FCSTD DOCUMENT  (FreeCAD 0.19R)
Label: threaded_ass2
License: All rights reserved
LicenseURL: http://en.wikipedia.org/wiki/All_rights_reserved
objects: Part::FeaturePython×42, Part::Feature×40, Part::Compound×26
note: 108 computed .brp shape members not serialized (recipe doc carries the construction recipe); baked Part::Feature solids carry a one-line shape summary decoded from their .brp

FEATURE [Part::Feature] Fillet001  label="endplate1b_chamf"
  shape: bbox 100 x 64 x 15 mm, 27 faces (baked)
FEATURE [Part::Feature] Fillet002  label="mountplate3b_chamf"
  Placement = pos=(0,0,455) rot=(0,0,1;0rad)
  shape: bbox 100 x 64 x 15 mm, 39 faces (baked)
FEATURE [Part::Feature] Pad001  label="shaft8x480"
  Placement = pos=(18,42.85,-5) rot=(0,0,1;0rad)
  shape: bbox 8 x 8 x 480 mm, 3 faces (baked)
FEATURE [Part::Feature] Pad002  label="shaft8x481"
  Placement = pos=(82,42.85,-5) rot=(0,0,1;0rad)
  shape: bbox 8 x 8 x 480 mm, 3 faces (baked)
FEATURE [Part::Feature] Fusion001  label="trapthread"
  Placement = pos=(50,42.85,-42) rot=(0,0,1;0rad)
  shape: bbox 12.27 x 13.21 x 480 mm, 558 faces (baked)
FEATURE [Part::Feature] Fusion001001001  label="nema17"
  Placement = pos=(50,42.85,510) rot=(0,1,0;3.14159rad)
  shape: bbox 48 x 42.3 x 60.1 mm, 110 faces (baked)
FEATURE [Part::Feature] Chamfer001  label="608zz"
  Placement = pos=(50,42.85,11) rot=(1,0,0;1.5708rad)
  shape: bbox 22 x 22 x 7 mm, 14 faces (baked)
FEATURE [Part::Feature] Body007  label="m6nutplate005"
  Placement = pos=(15,15,-3.5) rot=(0,0,-1;1.5708rad)
  shape: bbox 10 x 10 x 3 mm, 9 faces (baked)
FEATURE [Part::FeaturePython] b_tslot40_001_007  label="tslot40_Pocket001_008"  # a2plus imported part (geometry in sourceFile) (typed FeaturePython)
  Placement = pos=(60,10,15) rot=(-1,0,0;1.5708rad)
  Visibility1 = false
  Visibility11 = true
  a2p_Version = V0.1
  fixedPosition = false
  objectType = a2pPart
  sourceFile = .\Neuer Ordner (3)\tslot40.fcstd
  sourcePart = Pocket001
  subassemblyImport = false
  timeLastImport = 1585500225
  updateColors = true
FEATURE [Part::Feature] Body008  label="m6nutplate006"
  Placement = pos=(15,15,-3.5) rot=(0,0,-1;1.5708rad)
  shape: bbox 10 x 10 x 3 mm, 9 faces (baked)
FEATURE [Part::Feature] Pocket004003  label="tslot8con002"
  Placement = pos=(70,10,5) rot=(0,-1,0;1.5708rad)
  shape: bbox 80 x 20 x 20 mm, 150 faces (baked)
FEATURE [Part::Feature] Screw009  label="M6x16-Screw005"
  Placement = pos=(20,10,-16) rot=(1,0,0;3.14159rad)
  shape: bbox 10.5 x 10.5 x 19.3 mm, 15 faces (baked)
FEATURE [Part::Compound] Compound006  label="nutscrew020"
  Links = -> [Screw009,Body007]
  Placement = pos=(20,20,430) rot=(1,0,0;3.14159rad)
FEATURE [Part::FeaturePython] b_tslot40_001_010  label="tslot40_Pocket001_011"  # a2plus imported part (geometry in sourceFile) (typed FeaturePython)
  Placement = pos=(0,10,15) rot=(-1,0,0;1.5708rad)
  Visibility1 = false
  Visibility11 = true
  a2p_Version = V0.1
  fixedPosition = false
  objectType = a2pPart
  sourceFile = .\Neuer Ordner (3)\tslot40.fcstd
  sourcePart = Pocket001
  subassemblyImport = false
  timeLastImport = 1585500225
  updateColors = true
FEATURE [Part::Feature] Screw010  label="M6x16-Screw006"
  Placement = pos=(20,10,-16) rot=(1,0,0;3.14159rad)
  shape: bbox 10.5 x 10.5 x 19.3 mm, 15 faces (baked)
FEATURE [Part::Feature] Screw011  label="M6x40-Screw005"
  Placement = pos=(0,10,444) rot=(0,0,1;0rad)
  shape: bbox 10 x 10 x 46 mm, 19 faces (baked)
FEATURE [Part::Feature] Screw012  label="M6x40-Screw006"
  Placement = pos=(60,10,444) rot=(0,0,1;0rad)
  shape: bbox 10 x 10 x 46 mm, 19 faces (baked)
FEATURE [Part::Feature] Body009  label="m6nutplate007"
  Placement = pos=(15,15,-3.5) rot=(0,0,-1;1.5708rad)
  shape: bbox 10 x 10 x 3 mm, 9 faces (baked)
FEATURE [Part::Feature] Pocket004004  label="tslot8con003"
  Placement = pos=(70,10,425) rot=(0.707107,0,-0.707107;3.14159rad)
  shape: bbox 80 x 20 x 20 mm, 150 faces (baked)
FEATURE [Part::Feature] Body010  label="m6nutplate008"
  Placement = pos=(15,15,-3.5) rot=(0,0,-1;1.5708rad)
  shape: bbox 10 x 10 x 3 mm, 9 faces (baked)
FEATURE [Part::Compound] Compound009  label="nutscrew023"
  Links = -> [Screw010,Body010]
FEATURE [Part::Feature] Screw013  label="M6x40-Screw007"
  Placement = pos=(0,10,-14) rot=(1,0,0;3.14159rad)
  shape: bbox 10 x 10 x 46 mm, 19 faces (baked)
FEATURE [Part::Feature] Screw014  label="M6x40-Screw008"
  Placement = pos=(60,10,-14) rot=(1,0,0;3.14159rad)
  shape: bbox 10 x 10 x 46 mm, 19 faces (baked)
FEATURE [Part::Feature] Screw015  label="M6x16-Screw007"
  Placement = pos=(20,10,-16) rot=(1,0,0;3.14159rad)
  shape: bbox 10.5 x 10.5 x 19.3 mm, 15 faces (baked)
FEATURE [Part::Compound] Compound008  label="nutscrew022"
  Links = -> [Screw015,Body008]
  Placement = pos=(0,20,430) rot=(1,0,0;3.14159rad)
FEATURE [Part::Feature] Screw016  label="M6x16-Screw008"
  Placement = pos=(20,10,-16) rot=(1,0,0;3.14159rad)
  shape: bbox 10.5 x 10.5 x 19.3 mm, 15 faces (baked)
FEATURE [Part::Compound] Compound007  label="nutscrew021"
  Links = -> [Screw016,Body009]
  Placement = pos=(20,0,0) rot=(0,0,1;0rad)
FEATURE [Part::Compound] Compound010  label="frame_ass"
  Links = -> [b_tslot40_001_007,b_tslot40_001_010,Pocket004003,Pocket004004,Screw011,Screw012,Screw014,Screw013,Compound009,Compound007,Compound006,Compound008]
  Placement = pos=(20,0,20) rot=(0,0,1;0rad)
FEATURE [Part::Feature] difference001001  label="shaftcollar8mm"
  Placement = pos=(18,43,470) rot=(0,0,1;0rad)
  shape: bbox 20 x 19.97 x 8 mm, 16 faces (baked)
FEATURE [Part::Feature] difference001002  label="shaftcollar8mm001"
  Placement = pos=(82,43,470) rot=(0,0,1;0rad)
  shape: bbox 20 x 19.97 x 8 mm, 16 faces (baked)
FEATURE [Part::Feature] difference001003  label="shaftcollar8mm002"
  Placement = pos=(18,43,446.8) rot=(0,0,1;0rad)
  shape: bbox 20 x 19.97 x 8 mm, 16 faces (baked)
FEATURE [Part::Feature] difference001004  label="shaftcollar8mm003"
  Placement = pos=(82,43,446.8) rot=(0,0,1;0rad)
  shape: bbox 20 x 19.97 x 8 mm, 16 faces (baked)
FEATURE [Part::Feature] difference001005  label="shaftcollar8mm004"
  Placement = pos=(18,43,470) rot=(0,0,1;0rad)
  shape: bbox 20 x 19.97 x 8 mm, 16 faces (baked)
FEATURE [Part::Feature] difference001006  label="shaftcollar8mm005"
  Placement = pos=(82,43,470) rot=(0,0,1;0rad)
  shape: bbox 20 x 19.97 x 8 mm, 16 faces (baked)
FEATURE [Part::Feature] difference001007  label="shaftcollar8mm006"
  Placement = pos=(18,43,446.8) rot=(0,0,1;0rad)
  shape: bbox 20 x 19.97 x 8 mm, 16 faces (baked)
FEATURE [Part::Feature] difference001008  label="shaftcollar8mm007"
  Placement = pos=(82,43,446.8) rot=(0,0,1;0rad)
  shape: bbox 20 x 19.97 x 8 mm, 16 faces (baked)
FEATURE [Part::Compound] Compound  label="shaftcollars"
  Links = -> [difference001005,difference001006,difference001007,difference001008]
  Placement = pos=(0,0,-455) rot=(0,0,1;0rad)
FEATURE [Part::Compound] Compound011  label="shaftcollars2"
  Links = -> [difference001001,difference001002,difference001003,difference001004]
FEATURE [Part::FeaturePython] Screw  label="M3x16-Screw"  # Fasteners workbench fastener (typed FeaturePython)
  Placement = pos=(34.5,27,458) rot=(0,1,0;3.14159rad)
  Visibility1 = false
  diameter = 4
  invert = false
  length = 6
  matchOuter = false
  offset = 0
  thread = false
  type = 15
FEATURE [Part::FeaturePython] Screw017  label="M3x16-Screw001"  # Fasteners workbench fastener (typed FeaturePython)
  Placement = pos=(65.5,27,458) rot=(0,1,0;3.14159rad)
  Visibility1 = false
  diameter = 4
  invert = false
  length = 6
  matchOuter = false
  offset = 0
  thread = false
  type = 15
FEATURE [Part::FeaturePython] Screw018  label="M3x16-Screw002"  # Fasteners workbench fastener (typed FeaturePython)
  Placement = pos=(34.5,58,458) rot=(0,1,0;3.14159rad)
  Visibility1 = false
  diameter = 4
  invert = false
  length = 6
  matchOuter = false
  offset = 0
  thread = false
  type = 15
FEATURE [Part::FeaturePython] Screw019  label="M3x16-Screw003"  # Fasteners workbench fastener (typed FeaturePython)
  Placement = pos=(65.5,58,458) rot=(0,1,0;3.14159rad)
  Visibility1 = false
  diameter = 4
  invert = false
  length = 6
  matchOuter = false
  offset = 0
  thread = false
  type = 15
FEATURE [Part::Compound] Compound012  label="m3x16s"
  Links = -> [Screw,Screw017,Screw018,Screw019]
FEATURE [Part::FeaturePython] Screw020  label="M4x35-Screw001"  # Fasteners workbench fastener (typed FeaturePython)
  Placement = pos=(65,37,6) rot=(0,0,1;0rad)
  Visibility1 = false
  diameter = 5
  invert = false
  length = 9
  matchOuter = false
  offset = 0
  thread = false
  type = 15
FEATURE [Part::FeaturePython] Screw021  label="M4x12-Screw011"  # Fasteners workbench fastener (typed FeaturePython)
  Placement = pos=(6,6,6) rot=(0,0,1;0rad)
  Visibility1 = false
  diameter = 5
  invert = false
  length = 3
  matchOuter = false
  offset = 0
  thread = false
  type = 15
FEATURE [Part::FeaturePython] Screw022  label="M4x12-Screw014"  # Fasteners workbench fastener (typed FeaturePython)
  Placement = pos=(30,24,6) rot=(0,0,1;0rad)
  Visibility1 = false
  diameter = 5
  invert = false
  length = 3
  matchOuter = false
  offset = 0
  thread = false
  type = 15
FEATURE [Part::FeaturePython] Nut010  label="M3-Nut002"  # Fasteners workbench fastener (typed FeaturePython)
  Placement = pos=(50,54.5,-19) rot=(1,0,0;1.5708rad)
  Visibility1 = false
  diameter = 4
  invert = false
  matchOuter = false
  offset = 0
  thread = false
  type = 4
FEATURE [Part::Feature] Revolution002  label="LM8UU001"
  Placement = pos=(0,-15,-10.5) rot=(1,0,0;3.14159rad)
  shape: bbox 15 x 24 x 15 mm, 20 faces (baked)
FEATURE [Part::FeaturePython] Screw023  label="M4x12-Screw"  # Fasteners workbench fastener (typed FeaturePython)
  Placement = pos=(6,6,6) rot=(0,0,1;0rad)
  Visibility1 = false
  diameter = 5
  invert = false
  length = 3
  matchOuter = false
  offset = 0
  thread = false
  type = 15
FEATURE [Part::FeaturePython] Screw024  label="M3x20-Screw003"  # Fasteners workbench fastener (typed FeaturePython)
  Placement = pos=(50,37,-19) rot=(1,0,0;1.5708rad)
  Visibility1 = false
  diameter = 4
  invert = false
  length = 7
  matchOuter = false
  offset = 0
  thread = false
  type = 15
FEATURE [Part::Feature] Chamfer002001  label="nutblock"
  Placement = pos=(25,32,-22) rot=(0,0,1;0rad)
  shape: bbox 50 x 20 x 22 mm, 53 faces (baked)
FEATURE [Part::FeaturePython] Screw003  label="M4x12-Screw003"  # Fasteners workbench fastener (typed FeaturePython)
  Placement = pos=(6,24,6) rot=(0,0,1;0rad)
  Visibility1 = false
  diameter = 5
  invert = false
  length = 3
  matchOuter = false
  offset = 0
  thread = false
  type = 15
FEATURE [Part::FeaturePython] Nut007  label="M6-Nut003"  # Fasteners workbench fastener (typed FeaturePython)
  Placement = pos=(80,62,0) rot=(0,0,1;0rad)
  Visibility1 = false
  diameter = 2
  invert = false
  matchOuter = false
  offset = 0
  thread = false
  type = 2
FEATURE [Part::FeaturePython] Nut003  label="M4-Nut002"  # Fasteners workbench fastener (typed FeaturePython)
  Placement = pos=(65,47,-25) rot=(0,0,1;0rad)
  Visibility1 = false
  diameter = 6
  invert = false
  matchOuter = false
  offset = 0
  thread = false
  type = 4
FEATURE [Part::Feature] Cut001  label="trapeznut"
  Placement = pos=(50,35,-11) rot=(0,0,1;1.5708rad)
  shape: bbox 22 x 24 x 22 mm, 53 faces (baked)
FEATURE [Part::FeaturePython] Nut  label="M6-Nut"  # Fasteners workbench fastener (typed FeaturePython)
  Placement = pos=(20,22,0) rot=(0,0,1;0rad)
  Visibility1 = false
  diameter = 2
  invert = false
  matchOuter = false
  offset = 0
  thread = false
  type = 2
FEATURE [Part::FeaturePython] Nut002  label="M4-Nut001"  # Fasteners workbench fastener (typed FeaturePython)
  Placement = pos=(35,47,-25) rot=(0,0,1;0rad)
  Visibility1 = false
  diameter = 6
  invert = false
  matchOuter = false
  offset = 0
  thread = false
  type = 4
FEATURE [Part::FeaturePython] Screw004  label="M4x12-Screw004"  # Fasteners workbench fastener (typed FeaturePython)
  Placement = pos=(30,6,6) rot=(0,0,1;0rad)
  Visibility1 = false
  diameter = 5
  invert = false
  length = 3
  matchOuter = false
  offset = 0
  thread = false
  type = 15
FEATURE [Part::FeaturePython] Nut009  label="M3-Nut001"  # Fasteners workbench fastener (typed FeaturePython)
  Placement = pos=(50,54.5,-19) rot=(1,0,0;1.5708rad)
  Visibility1 = false
  diameter = 4
  invert = false
  matchOuter = false
  offset = 0
  thread = false
  type = 4
FEATURE [Part::FeaturePython] Screw002  label="M4x12-Screw002"  # Fasteners workbench fastener (typed FeaturePython)
  Placement = pos=(30,24,6) rot=(0,0,1;0rad)
  Visibility1 = false
  diameter = 5
  invert = false
  length = 3
  matchOuter = false
  offset = 0
  thread = false
  type = 15
FEATURE [Part::FeaturePython] Screw008  label="M4x12-Screw008"  # Fasteners workbench fastener (typed FeaturePython)
  Placement = pos=(30,6,6) rot=(0,0,1;0rad)
  Visibility1 = false
  diameter = 5
  invert = false
  length = 3
  matchOuter = false
  offset = 0
  thread = false
  type = 15
FEATURE [Part::FeaturePython] Screw025  label="M4x12-Screw015"  # Fasteners workbench fastener (typed FeaturePython)
  Placement = pos=(6,24,6) rot=(0,0,1;0rad)
  Visibility1 = false
  diameter = 5
  invert = false
  length = 3
  matchOuter = false
  offset = 0
  thread = false
  type = 15
FEATURE [Part::FeaturePython] Screw026  label="M3x20-Screw002"  # Fasteners workbench fastener (typed FeaturePython)
  Placement = pos=(50,37,-19) rot=(1,0,0;1.5708rad)
  Visibility1 = false
  diameter = 4
  invert = false
  length = 7
  matchOuter = false
  offset = 0
  thread = false
  type = 15
FEATURE [Part::Compound] Compound013  label="m3x20screwnut002"
  Links = -> [Screw026,Nut010]
FEATURE [Part::FeaturePython] Nut004  label="M4-Nut003"  # Fasteners workbench fastener (typed FeaturePython)
  Placement = pos=(65,37,-25) rot=(0,0,1;0rad)
  Visibility1 = false
  diameter = 6
  invert = false
  matchOuter = false
  offset = 0
  thread = false
  type = 4
FEATURE [Part::Feature] Body003  label="SC8UU002"
  shape: bbox 34 x 30 x 22 mm, 85 faces (baked)
FEATURE [Part::FeaturePython] Screw027  label="M3x20-Screw"  # Fasteners workbench fastener (typed FeaturePython)
  Placement = pos=(50,37,-19) rot=(1,0,0;1.5708rad)
  Visibility1 = false
  diameter = 4
  invert = false
  length = 7
  matchOuter = false
  offset = 0
  thread = false
  type = 15
FEATURE [Part::Feature] Body001  label="SC8UU"
  shape: bbox 34 x 30 x 22 mm, 85 faces (baked)
FEATURE [Part::Feature] Body004  label="SC8UU003"
  shape: bbox 34 x 30 x 22 mm, 85 faces (baked)
FEATURE [Part::Feature] Revolution003  label="LM8UU002"
  Placement = pos=(0,-15,-10.5) rot=(1,0,0;3.14159rad)
  shape: bbox 15 x 24 x 15 mm, 20 faces (baked)
FEATURE [Part::FeaturePython] Screw028  label="M4x12-Screw013"  # Fasteners workbench fastener (typed FeaturePython)
  Placement = pos=(30,6,6) rot=(0,0,1;0rad)
  Visibility1 = false
  diameter = 5
  invert = false
  length = 3
  matchOuter = false
  offset = 0
  thread = false
  type = 15
FEATURE [Part::FeaturePython] Nut001  label="M4-Nut"  # Fasteners workbench fastener (typed FeaturePython)
  Placement = pos=(35,37,-25) rot=(0,0,1;0rad)
  Visibility1 = false
  diameter = 6
  invert = false
  matchOuter = false
  offset = 0
  thread = false
  type = 4
FEATURE [Part::Compound] Compound014  label="m4nuts"
  Links = -> [Nut001,Nut002,Nut003,Nut004]
FEATURE [Part::FeaturePython] Screw029  label="M4x12-Screw012"  # Fasteners workbench fastener (typed FeaturePython)
  Placement = pos=(6,6,6) rot=(0,0,1;0rad)
  Visibility1 = false
  diameter = 5
  invert = false
  length = 3
  matchOuter = false
  offset = 0
  thread = false
  type = 15
FEATURE [Part::Compound] Compound003  label="m4x12_4er003"
  Links = -> [Screw029,Screw028,Screw022,Screw025]
  Placement = pos=(0,54,0) rot=(0,0,1;0rad)
FEATURE [Part::FeaturePython] Screw005  label="M4x12-Screw005"  # Fasteners workbench fastener (typed FeaturePython)
  Placement = pos=(6,6,6) rot=(0,0,1;0rad)
  Visibility1 = false
  diameter = 5
  invert = false
  length = 3
  matchOuter = false
  offset = 0
  thread = false
  type = 15
FEATURE [Part::Feature] Revolution001  label="LM8UU"
  Placement = pos=(0,-15,-10.5) rot=(1,0,0;3.14159rad)
  shape: bbox 15 x 24 x 15 mm, 20 faces (baked)
FEATURE [Part::Compound] Compound019  label="SC8UU+LM8UU"
  Links = -> [Revolution001,Body001]
  Placement = pos=(18,30,-0.5) rot=(0,0,1;0rad)
FEATURE [Part::Feature] Revolution004  label="LM8UU003"
  Placement = pos=(0,-15,-10.5) rot=(1,0,0;3.14159rad)
  shape: bbox 15 x 24 x 15 mm, 20 faces (baked)
FEATURE [Part::FeaturePython] Screw030  label="M4x35-Screw002"  # Fasteners workbench fastener (typed FeaturePython)
  Placement = pos=(65,47,6) rot=(0,0,1;0rad)
  Visibility1 = false
  diameter = 5
  invert = false
  length = 9
  matchOuter = false
  offset = 0
  thread = false
  type = 15
FEATURE [Part::FeaturePython] Screw031  label="M4x35-Screw"  # Fasteners workbench fastener (typed FeaturePython)
  Placement = pos=(35,37,6) rot=(0,0,1;0rad)
  Visibility1 = false
  diameter = 5
  invert = false
  length = 9
  matchOuter = false
  offset = 0
  thread = false
  type = 15
FEATURE [Part::FeaturePython] Screw007  label="M4x12-Screw007"  # Fasteners workbench fastener (typed FeaturePython)
  Placement = pos=(6,24,6) rot=(0,0,1;0rad)
  Visibility1 = false
  diameter = 5
  invert = false
  length = 3
  matchOuter = false
  offset = 0
  thread = false
  type = 15
FEATURE [Part::Feature] Fillet002001  label="carriageplate2"
  shape: bbox 100.3 x 84.33 x 10 mm, 118 faces (baked)
FEATURE [Part::FeaturePython] Screw032  label="M4x12-Screw009"  # Fasteners workbench fastener (typed FeaturePython)
  Placement = pos=(30,24,6) rot=(0,0,1;0rad)
  Visibility1 = false
  diameter = 5
  invert = false
  length = 3
  matchOuter = false
  offset = 0
  thread = false
  type = 15
FEATURE [Part::FeaturePython] Nut008  label="M3-Nut"  # Fasteners workbench fastener (typed FeaturePython)
  Placement = pos=(50,54.5,-19) rot=(1,0,0;1.5708rad)
  Visibility1 = false
  diameter = 4
  invert = false
  matchOuter = false
  offset = 0
  thread = false
  type = 4
FEATURE [Part::Compound] Compound021  label="m3x20screwnut"
  Links = -> [Screw027,Nut008]
  Placement = pos=(8,0,8) rot=(0,0,1;0rad)
FEATURE [Part::FeaturePython] Screw006  label="M4x12-Screw006"  # Fasteners workbench fastener (typed FeaturePython)
  Placement = pos=(30,24,6) rot=(0,0,1;0rad)
  Visibility1 = false
  diameter = 5
  invert = false
  length = 3
  matchOuter = false
  offset = 0
  thread = false
  type = 15
FEATURE [Part::Compound] Compound001  label="m4x12_4er001"
  Links = -> [Screw005,Screw004,Screw006,Screw007]
  Placement = pos=(64,0,0) rot=(0,0,1;0rad)
FEATURE [Part::FeaturePython] Screw001  label="M4x12-Screw001"  # Fasteners workbench fastener (typed FeaturePython)
  Placement = pos=(30,6,6) rot=(0,0,1;0rad)
  Visibility1 = false
  diameter = 5
  invert = false
  length = 3
  matchOuter = false
  offset = 0
  thread = false
  type = 15
FEATURE [Part::Compound] Compound018  label="m4x12_4er"
  Links = -> [Screw023,Screw001,Screw002,Screw003]
FEATURE [Part::Feature] Body002  label="SC8UU001"
  shape: bbox 34 x 30 x 22 mm, 85 faces (baked)
FEATURE [Part::Compound] Compound024  label="SC8UU+LM8UU001"
  Links = -> [Revolution002,Body002]
  Placement = pos=(82,30,-0.5) rot=(0,0,1;0rad)
FEATURE [Part::FeaturePython] Nut006  label="M6-Nut004"  # Fasteners workbench fastener (typed FeaturePython)
  Placement = pos=(20,62,0) rot=(0,0,1;0rad)
  Visibility1 = false
  diameter = 2
  invert = false
  matchOuter = false
  offset = 0
  thread = false
  type = 2
FEATURE [Part::FeaturePython] Nut011  label="M3-Nut003"  # Fasteners workbench fastener (typed FeaturePython)
  Placement = pos=(50,54.5,-19) rot=(1,0,0;1.5708rad)
  Visibility1 = false
  diameter = 4
  invert = false
  matchOuter = false
  offset = 0
  thread = false
  type = 4
FEATURE [Part::Compound] Compound023  label="m3x20screwnut003"
  Links = -> [Screw024,Nut011]
  Placement = pos=(-8,0,8) rot=(0,0,1;0rad)
FEATURE [Part::Compound] Compound016  label="SC8UU+LM8UU003"
  Links = -> [Revolution004,Body004]
  Placement = pos=(18,84,-0.5) rot=(0,0,1;0rad)
FEATURE [Part::FeaturePython] Screw033  label="M3x20-Screw001"  # Fasteners workbench fastener (typed FeaturePython)
  Placement = pos=(50,37,-19) rot=(1,0,0;1.5708rad)
  Visibility1 = false
  diameter = 4
  invert = false
  length = 7
  matchOuter = false
  offset = 0
  thread = false
  type = 15
FEATURE [Part::Compound] Compound020  label="m3x20screwnut001"
  Links = -> [Screw033,Nut009]
  Placement = pos=(0,0,16) rot=(0,0,1;0rad)
FEATURE [Part::Compound] Compound022  label="m3x20screwnuts"
  Links = -> [Compound021,Compound020,Compound013,Compound023]
FEATURE [Part::Compound] Compound015  label="SC8UU+LM8UU002"
  Links = -> [Revolution003,Body003]
  Placement = pos=(82,84,-0.5) rot=(0,0,1;0rad)
FEATURE [Part::FeaturePython] Nut005  label="M6-Nut001"  # Fasteners workbench fastener (typed FeaturePython)
  Placement = pos=(80,22,0) rot=(0,0,1;0rad)
  Visibility1 = false
  diameter = 2
  invert = false
  matchOuter = false
  offset = 0
  thread = false
  type = 2
FEATURE [Part::Compound] Compound025  label="m6nuts"
  Links = -> [Nut,Nut005,Nut006,Nut007]
FEATURE [Part::FeaturePython] Screw034  label="M4x12-Screw010"  # Fasteners workbench fastener (typed FeaturePython)
  Placement = pos=(6,24,6) rot=(0,0,1;0rad)
  Visibility1 = false
  diameter = 5
  invert = false
  length = 3
  matchOuter = false
  offset = 0
  thread = false
  type = 15
FEATURE [Part::Compound] Compound002  label="m4x12_4er002"
  Links = -> [Screw021,Screw008,Screw032,Screw034]
  Placement = pos=(64,54,0) rot=(0,0,1;0rad)
FEATURE [Part::Compound] Compound004  label="m4x12ers"
  Links = -> [Compound018,Compound001,Compound002,Compound003]
FEATURE [Part::FeaturePython] Screw035  label="M4x35-Screw003"  # Fasteners workbench fastener (typed FeaturePython)
  Placement = pos=(35,47,6) rot=(0,0,1;0rad)
  Visibility1 = false
  diameter = 5
  invert = false
  length = 9
  matchOuter = false
  offset = 0
  thread = false
  type = 15
FEATURE [Part::Compound] Compound005  label="m4x35ers"
  Links = -> [Screw031,Screw020,Screw030,Screw035]
FEATURE [Part::Compound] Compound017  label="carriage_ass4-Modul"
  Links = -> [Chamfer002001,Cut001,Compound004,Compound005,Compound014,Compound025,Compound022,Fillet002001,Compound019,Compound024,Compound015,Compound016]
  Placement = pos=(0,53.9,300) rot=(1,0,0;4.71239rad)
